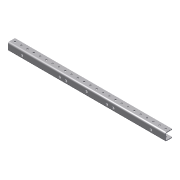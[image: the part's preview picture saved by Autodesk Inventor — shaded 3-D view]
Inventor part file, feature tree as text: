
AUTODESK INVENTOR PART (.ipt)
format: ipt  version: 2013 (Build 170138000, 138)  size: 227,840 bytes
history: native  units: in
note: dims shown in document units (in); Inventor stores cm internally (conversion verified against a paired STEP export)
features: projected_geometry x8, extrude x3, sketch x3, other x1, mirror x1, imported_body x1
ambient origin geometry x8: Origin, YZ Plane, XZ Plane, XY Plane, X Axis, Y Axis, Z Axis, Center Point
feature tree (17):
  other  "Short C Channel for drive1"
  extrude  "Extrusion1"  TaperAngle=0.0deg  [1 undecoded]
  extrude  "Extrusion2"  Depth=0.15in
  extrude  "Extrusion3"  Depth=1.0in TaperAngle=0.0deg
  mirror  "Mirror1"
  imported_body  "Base1"
  sketch  "Sketch1"  dims[d1=0.0in d3=0.0in]
  projected_geometry  "Projected Loop1"
  projected_geometry  "Projected Loop2"
  projected_geometry  "Projected Loop3"
  projected_geometry  "Projected Loop4"
  sketch  "Sketch2"  dims[d4=0.38in d5=0.15in]
  projected_geometry  "Projected Loop5"
  projected_geometry  "Projected Loop6"
  projected_geometry  "Projected Loop7"
  projected_geometry  "Projected Loop8"
  sketch  "Sketch3"  dims[d6=10.25in d7=1.0in d8=0.0in]
note: 1 required parameter value undecoded (feature->parameter linkage not recoverable at this tier; creation-order binding heuristic only, values carry confidence <= 0.55)
